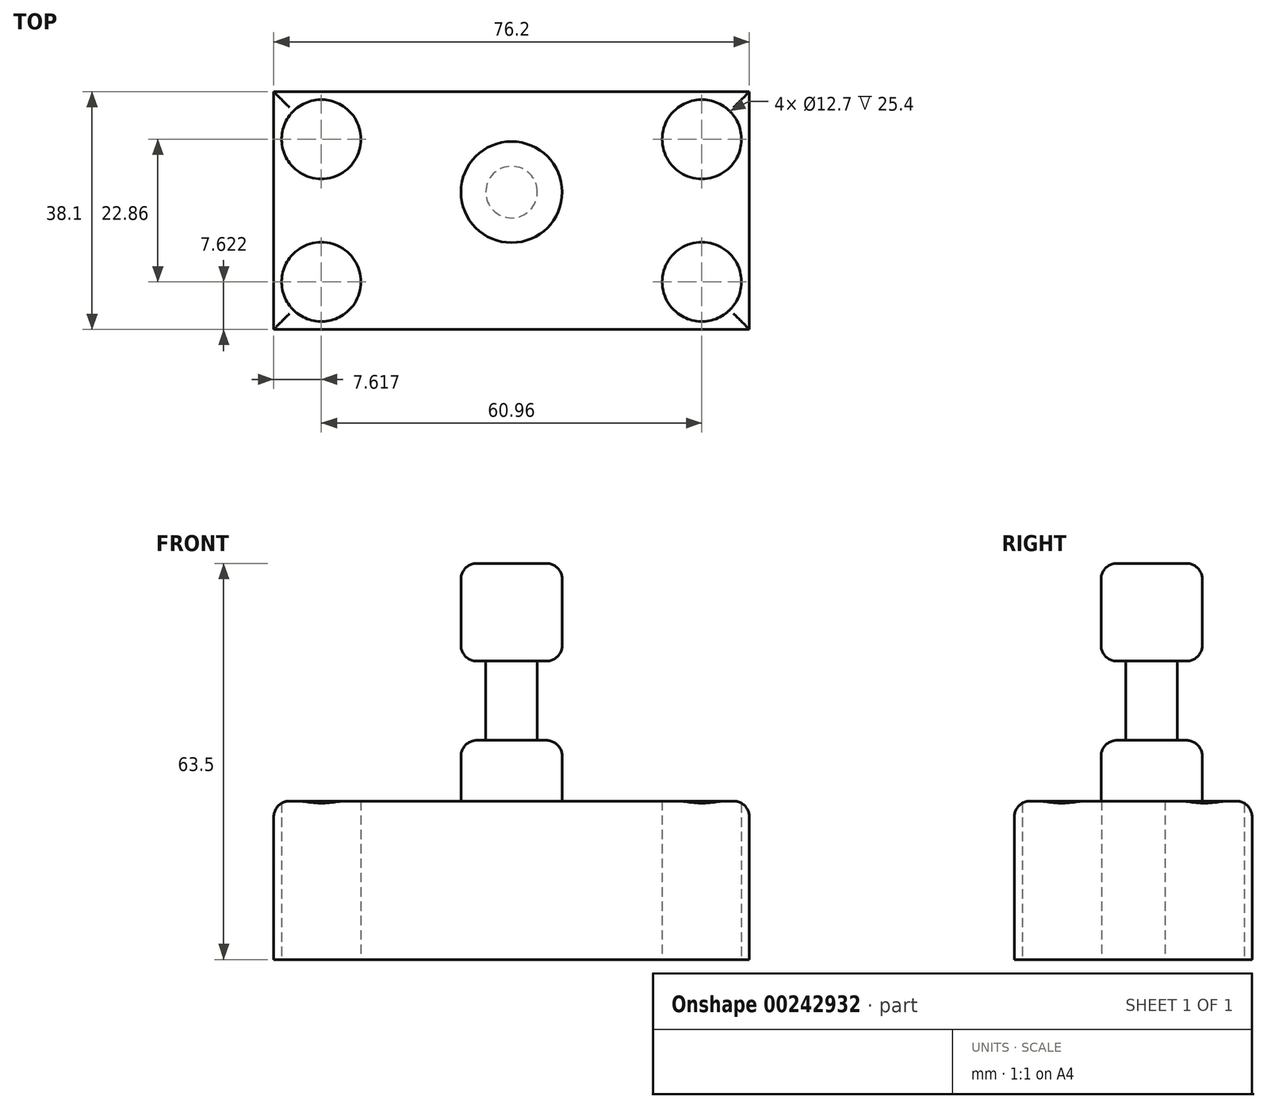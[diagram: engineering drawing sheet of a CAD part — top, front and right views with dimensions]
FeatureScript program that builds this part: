
annotation { "Feature Type Name" : "Feature", "Feature Type Description" : "" }
export const myFeature = defineFeature(function(context is Context, id is Id, definition is map)
    precondition{}
    {
        {
            var Q0;
            Q0=qCreatedBy(makeId("Top.planeOp"),FACE);
            var sketch = newSketch(context, id + "F0", { "sketchPlane" : qUnion([Q0])});
            skLineSegment(sketch, "E0.bottom", {"start": v(-38.1, 16.1) * mm, "end": v(38.1, 16.1) * mm});
            skLineSegment(sketch, "E0.top", {"start": v(-38.1, -22) * mm, "end": v(38.1, -22) * mm});
            skLineSegment(sketch, "E0.left", {"start": v(-38.1, 16.1) * mm, "end": v(-38.1, -22) * mm});
            skLineSegment(sketch, "E0.right", {"start": v(38.1, 16.1) * mm, "end": v(38.1, -22) * mm});
            skSolve(sketch);
        }
        {
            var Q0;
            Q0 = qSketchRegion(id + "F0", true);
            extrude(context, id + "F1", {"entities" : qUnion([Q0]), "depth" : 25.4 * mm});
        }
        {
            var Q0;
            Q0=qCreatedBy(makeId("Top.planeOp"),FACE);
            var sketch = newSketch(context, id + "F2", { "sketchPlane" : qUnion([Q0])});
            skCircle(sketch, "E1", {"center": v(-30.48, 8.47) * mm, "radius": 6.35 * mm});
            skCircle(sketch, "E2", {"center": v(30.48, 8.47) * mm, "radius": 6.35 * mm});
            skCircle(sketch, "E3", {"center": v(-30.48, -14.39) * mm, "radius": 6.35 * mm});
            skCircle(sketch, "E4", {"center": v(30.48, -14.39) * mm, "radius": 6.35 * mm});
            skSolve(sketch);
        }
        {
            var Q0;
            Q0 = qSketchRegion(id + "F2", true);
            extrude(context, id + "F3", {"entities" : qUnion([Q0]), "operationType" : NewBodyOperationType.REMOVE, "depth" : 25.4 * mm});
        }
        {
            var Q0;
            Q0=makeQuery(id+"F1.opExtrude","CAP_FACE",FACE,{"disambiguationData":[OSD([sQuery(id+"F0.wireOp",EDGE,"E0.bottom"),sQuery(id+"F0.wireOp",EDGE,"E0.top"),sQuery(id+"F0.wireOp",EDGE,"E0.left"),sQuery(id+"F0.wireOp",EDGE,"E0.right")])],"isStart":false});
            var sketch = newSketch(context, id + "F4", { "sketchPlane" : qUnion([Q0])});
            skCircle(sketch, "E5", {"center": v(0, 0) * mm, "radius": 8.1 * mm});
            skSolve(sketch);
        }
        {
            var Q0;
            Q0 = qSketchRegion(id + "F4", true);
            extrude(context, id + "F5", {"entities" : qUnion([Q0]), "operationType" : NewBodyOperationType.ADD, "depth" : 38.1 * mm});
        }
        {
            var Q0;
            Q0=qCreatedBy(makeId("Front.planeOp"),FACE);
            var sketch = newSketch(context, id + "F6", { "sketchPlane" : qUnion([Q0])});
            skLineSegment(sketch, "E6.bottom", {"start": v(-16.83, 47.83) * mm, "end": v(-4.13, 47.83) * mm});
            skLineSegment(sketch, "E6.top", {"start": v(-16.83, 35.13) * mm, "end": v(-4.13, 35.13) * mm});
            skLineSegment(sketch, "E6.left", {"start": v(-16.83, 47.83) * mm, "end": v(-16.83, 35.13) * mm});
            skLineSegment(sketch, "E6.right", {"start": v(-4.13, 47.83) * mm, "end": v(-4.13, 35.13) * mm});
            skSolve(sketch);
        }
        {
            var Q0;
            Q0=makeQuery(id+"F6.imprint","IMPRINT",FACE,{"disambiguationData":[TD([[makeQuery(id+"F6.imprint","IMPRINT",EDGE,{"derivedFrom":sQuery(id+"F6.wireOp",EDGE,"E6.bottom")}),-1.0]])]});
            var Q1;
            Q1=makeQuery(id+"F5.opExtrude","SWEPT_FACE",FACE,{"disambiguationData":[OSD([sQuery(id+"F4.wireOp",EDGE,"E5")])]});
            revolve(context, id + "F7", {"operationType" : NewBodyOperationType.REMOVE, "entities" : qUnion([Q0]), "axis" : qUnion([Q1]), "revolveType" : RevolveType.FULL, "oppositeDirection" : true});
        }
        {
            var Q0;
            Q0=makeQuery(id+"F1.opExtrude","CAP_EDGE",EDGE,{"disambiguationData":[OSD([sQuery(id+"F0.wireOp",EDGE,"E0.left")])],"isStart":false});
            var Q1;
            Q1=makeQuery(id+"F1.opExtrude","CAP_EDGE",EDGE,{"disambiguationData":[OSD([sQuery(id+"F0.wireOp",EDGE,"E0.top")])],"isStart":false});
            var Q2;
            Q2=makeQuery(id+"F7.boolean.opBoolean","INTERSECT",EDGE,{"derivedFrom":[makeQuery(id+"F5.opExtrude","SWEPT_FACE",FACE,{"disambiguationData":[OSD([sQuery(id+"F4.wireOp",EDGE,"E5")])]}),makeQuery(id+"F7.opRevolve","SWEPT_FACE",FACE,{"disambiguationData":[OSD([sQuery(id+"F6.wireOp",EDGE,"E6.top")])]})]});
            var Q3;
            Q3=makeQuery(id+"F7.boolean.opBoolean","INTERSECT",EDGE,{"derivedFrom":[makeQuery(id+"F5.opExtrude","SWEPT_FACE",FACE,{"disambiguationData":[OSD([sQuery(id+"F4.wireOp",EDGE,"E5")])]}),makeQuery(id+"F7.opRevolve","SWEPT_FACE",FACE,{"disambiguationData":[OSD([sQuery(id+"F6.wireOp",EDGE,"E6.bottom")])]})]});
            var Q4;
            Q4=makeQuery(id+"F5.opExtrude","CAP_EDGE",EDGE,{"disambiguationData":[OSD([sQuery(id+"F4.wireOp",EDGE,"E5")])],"isStart":false});
            var Q5;
            Q5=makeQuery(id+"F5.opExtrude","CAP_EDGE",EDGE,{"disambiguationData":[OSD([sQuery(id+"F4.wireOp",EDGE,"E5")])],"isStart":true});
            var Q6;
            Q6=makeQuery(id+"F1.opExtrude","CAP_EDGE",EDGE,{"disambiguationData":[OSD([sQuery(id+"F0.wireOp",EDGE,"E0.bottom")])],"isStart":false});
            var Q7;
            Q7=makeQuery(id+"F1.opExtrude","CAP_EDGE",EDGE,{"disambiguationData":[OSD([sQuery(id+"F0.wireOp",EDGE,"E0.right")])],"isStart":false});
            fillet(context, id + "F8", {"entities" : qUnion([Q0, Q1, Q2, Q3, Q4, Q5, Q6, Q7]), "radius" : 2.54 * mm, "tangentPropagation" : true, "allowEdgeOverflow" : false});
        }
    });
